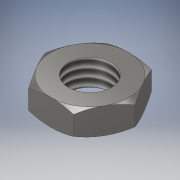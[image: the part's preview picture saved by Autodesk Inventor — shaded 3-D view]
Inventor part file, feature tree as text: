
AUTODESK INVENTOR PART (.ipt)
format: ipt  version: 2018 (Build 220112000, 112)  size: 149,504 bytes
history: native  units: in
note: dims shown in document units (in); Inventor stores cm internally (conversion verified against a paired STEP export)
features: sketch x2, extrude x1, revolve x1, hole x1, projected_geometry x1
ambient origin geometry x8: Origin, YZ Plane, XZ Plane, XY Plane, X Axis, Y Axis, Z Axis, Center Point
bodies: Solid1 (feature_tree)
feature tree (6):
  extrude  "Extrusion2"  Depth=0.75in
  revolve  "Revolution3"  Angle=90.0deg
  hole  "Hole1"  [1 undecoded]
  sketch  "Sketch3"  dims[d9=0.25in d10=0.0in d15=0.75in]
  sketch  "Sketch5"  dims[d16=30.0deg d17=90.0deg d30=1.0in d31=1.0in d20=0.417in d21=1.0in d22=0.375in d23=0.25in d24=0.5635in d25=1.385in d26=0.8108in d27=0.75in]
  projected_geometry  "Projected Loop2"
note: 1 required parameter value undecoded (feature->parameter linkage not recoverable at this tier; creation-order binding heuristic only, values carry confidence <= 0.55)
